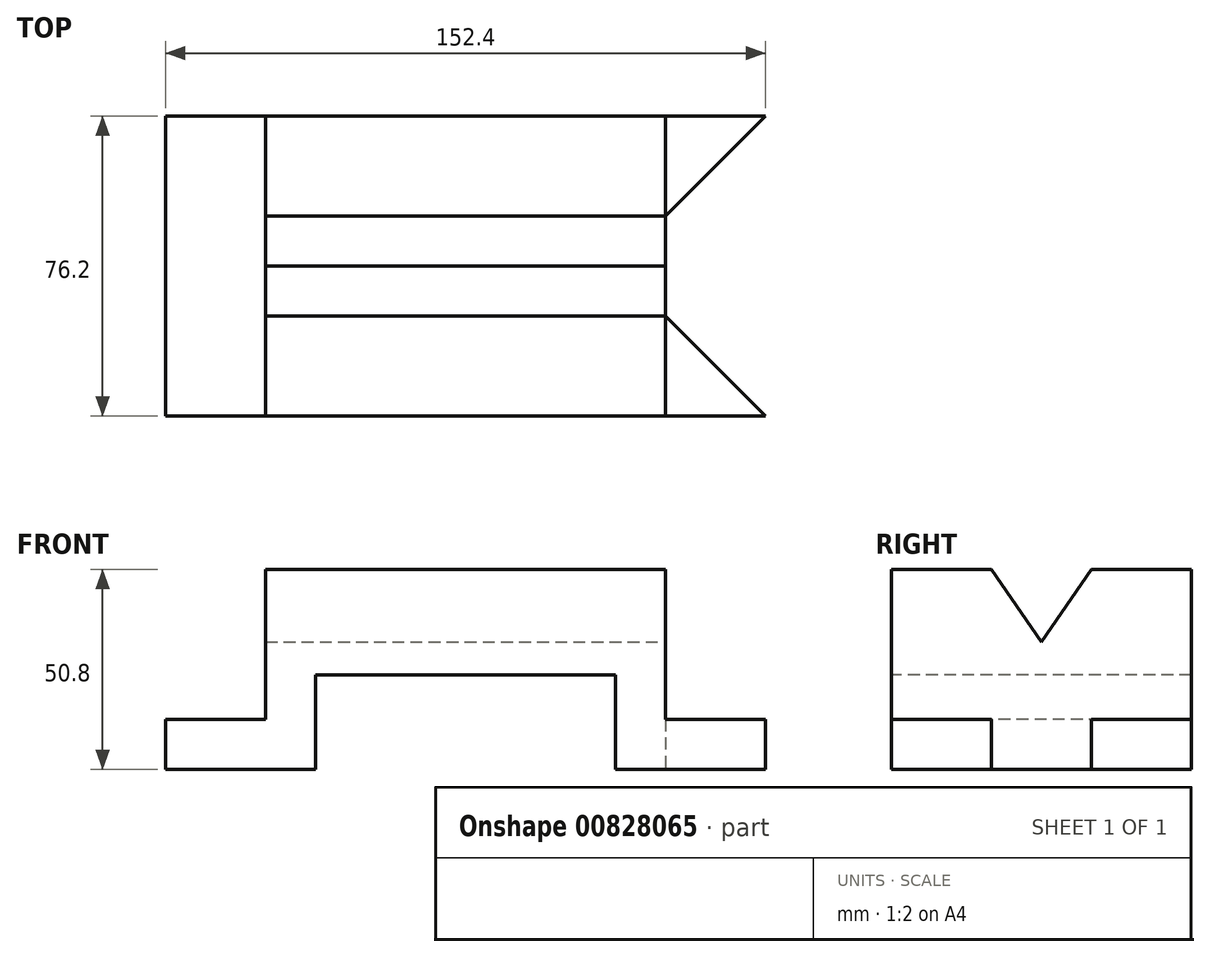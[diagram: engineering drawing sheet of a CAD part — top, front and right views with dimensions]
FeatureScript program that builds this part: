
annotation { "Feature Type Name" : "Feature", "Feature Type Description" : "" }
export const myFeature = defineFeature(function(context is Context, id is Id, definition is map)
    precondition{}
    {
        {
            var Q0;
            Q0=qCreatedBy(makeId("Top.planeOp"),FACE);
            var sketch = newSketch(context, id + "F0", { "sketchPlane" : qUnion([Q0])});
            skLineSegment(sketch, "E0", {"start": v(-81.58, 27.24) * mm, "end": v(-81.58, -48.96) * mm});
            skLineSegment(sketch, "E1", {"start": v(-81.58, -48.96) * mm, "end": v(70.82, -48.96) * mm});
            skLineSegment(sketch, "E2", {"start": v(70.82, -48.96) * mm, "end": v(45.42, -23.56) * mm});
            skLineSegment(sketch, "E3", {"start": v(45.42, -23.56) * mm, "end": v(45.42, 1.84) * mm});
            skLineSegment(sketch, "E4", {"start": v(45.42, 1.84) * mm, "end": v(70.82, 27.24) * mm});
            skLineSegment(sketch, "E5", {"start": v(70.82, 27.24) * mm, "end": v(-81.58, 27.24) * mm});
            skLineSegment(sketch, "E6", {"start": v(45.42, 1.84) * mm, "end": v(45.42, 27.24) * mm});
            skLineSegment(sketch, "E7", {"start": v(45.42, -23.56) * mm, "end": v(45.42, -48.96) * mm});
            skLineSegment(sketch, "E8", {"start": v(-56.18, 27.24) * mm, "end": v(-56.18, -48.96) * mm});
            skSolve(sketch);
        }
        {
            var Q0;
            {var subQ0=sQuery(id+"F0.wireOp",EDGE,"E0");Q0=makeQuery(id+"F0.imprint","IMPRINT",FACE,{"disambiguationData":[TD([[makeQuery(id+"F0.imprint","IMPRINT",EDGE,{"derivedFrom":subQ0}),1.0]])]});}
            extrude(context, id + "F1", {"entities" : qUnion([Q0]), "depth" : 12.7 * mm, "offsetDistance" : 25.4 * mm});
        }
        {
            var Q0;
            Q0=makeQuery(id+"F0.imprint","IMPRINT",FACE,{"disambiguationData":[TD([[makeQuery(id+"F0.imprint","IMPRINT",EDGE,{"derivedFrom":sQuery(id+"F0.wireOp",EDGE,"E3")}),1.0]])]});
            extrude(context, id + "F2", {"entities" : qUnion([Q0]), "operationType" : NewBodyOperationType.ADD, "depth" : 50.8 * mm, "offsetDistance" : 25.4 * mm});
        }
        {
            var Q0;
            {var subQ0=sQuery(id+"F0.wireOp",EDGE,"E4");Q0=makeQuery(id+"F0.imprint","IMPRINT",FACE,{"disambiguationData":[TD([[makeQuery(id+"F0.imprint","IMPRINT",EDGE,{"derivedFrom":subQ0}),1.0]])]});}
            var Q1;
            {var subQ0=sQuery(id+"F0.wireOp",EDGE,"E2");Q1=makeQuery(id+"F0.imprint","IMPRINT",FACE,{"disambiguationData":[TD([[makeQuery(id+"F0.imprint","IMPRINT",EDGE,{"derivedFrom":subQ0}),1.0]])]});}
            extrude(context, id + "F3", {"entities" : qUnion([Q0, Q1]), "operationType" : NewBodyOperationType.ADD, "depth" : 12.7 * mm, "offsetDistance" : 25.4 * mm});
        }
        {
            var Q0;
            Q0=makeQuery(id+"F2.opExtrude","SWEPT_FACE",FACE,{"disambiguationData":[OSD([sQuery(id+"F0.wireOp",EDGE,"E3"),sQuery(id+"F0.wireOp",EDGE,"E6"),sQuery(id+"F0.wireOp",EDGE,"E7")])]});
            var sketch = newSketch(context, id + "F4", { "sketchPlane" : qUnion([Q0])});
            skLineSegment(sketch, "E9", {"start": v(1.84, 50.8) * mm, "end": v(-10.85, 32.45) * mm});
            skLineSegment(sketch, "E10", {"start": v(-10.85, 32.45) * mm, "end": v(-23.56, 50.8) * mm});
            skSolve(sketch);
        }
        {
            var Q0;
            {var subQ0=sQuery(id+"F4.wireOp",EDGE,"E9");Q0=makeQuery(id+"F4.imprint","IMPRINT",FACE,{"disambiguationData":[TD([[makeQuery(id+"F4.imprint","IMPRINT",EDGE,{"derivedFrom":subQ0}),-1.0]])]});}
            extrude(context, id + "F5", {"entities" : qUnion([Q0]), "operationType" : NewBodyOperationType.REMOVE, "endBound" : BoundingType.THROUGH_ALL, "oppositeDirection" : true, "depth" : 25.4 * mm, "offsetDistance" : 25.4 * mm});
        }
        {
            var Q0;
            {var subQ0=sQuery(id+"F0.wireOp",EDGE,"E1");Q0=makeQuery(id+"F3.boolean.opBoolean","MERGE",FACE,{"derivedFrom":[makeQuery(id+"F2.boolean.opBoolean","MERGE",FACE,{"derivedFrom":[makeQuery(id+"F1.opExtrude","SWEPT_FACE",FACE,{"disambiguationData":[OSD([subQ0])]}),makeQuery(id+"F2.opExtrude","SWEPT_FACE",FACE,{"disambiguationData":[OSD([subQ0])]})]}),makeQuery(id+"F3.opExtrude","SWEPT_FACE",FACE,{"disambiguationData":[OSD([subQ0])]})]});}
            var sketch = newSketch(context, id + "F6", { "sketchPlane" : qUnion([Q0])});
            skLineSegment(sketch, "E11", {"start": v(-43.48, 0) * mm, "end": v(-43.48, 24.03) * mm});
            skLineSegment(sketch, "E12", {"start": v(-43.48, 24.03) * mm, "end": v(32.72, 24.03) * mm});
            skLineSegment(sketch, "E13", {"start": v(32.72, 24.03) * mm, "end": v(32.72, 0) * mm});
            skSolve(sketch);
        }
        {
            var Q0;
            {var subQ0=sQuery(id+"F6.wireOp",EDGE,"E11");Q0=makeQuery(id+"F6.imprint","IMPRINT",FACE,{"disambiguationData":[TD([[makeQuery(id+"F6.imprint","IMPRINT",EDGE,{"derivedFrom":subQ0}),-1.0]])]});}
            extrude(context, id + "F7", {"entities" : qUnion([Q0]), "operationType" : NewBodyOperationType.REMOVE, "endBound" : BoundingType.THROUGH_ALL, "oppositeDirection" : true, "depth" : 25.4 * mm, "offsetDistance" : 25.4 * mm});
        }
    });
